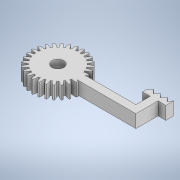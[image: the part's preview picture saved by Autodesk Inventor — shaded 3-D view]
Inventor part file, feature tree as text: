
AUTODESK INVENTOR PART (.ipt)
format: ipt  version: 2022 (Build 260153000, 153)  size: 456,704 bytes
history: native  units: in
note: dims shown in document units (in); Inventor stores cm internally (conversion verified against a paired STEP export)
features: extrude x16, sketch x16, pattern_circular x1
ambient origin geometry x8: Origin, YZ Plane, XZ Plane, XY Plane, X Axis, Y Axis, Z Axis, Center Point
bodies: Solid1 (feature_tree)
feature tree (33):
  extrude  "Extrusion1"  Depth=0.1575in
  pattern_circular  "Circular Pattern1"  Count=28 Angle=360.0deg
  extrude  "Extrusion6"  Depth=0.1969in
  extrude  "Extrusion7"  Depth=1.1811in
  extrude  "Extrusion8"  Depth=0.748in
  extrude  "Extrusion9"  Depth=0.1969in
  extrude  "Extrusion10"  Depth=0.0591in
  extrude  "Extrusion11"  Depth=0.0591in
  extrude  "Extrusion12"  Depth=0.3543in
  extrude  "Extrusion13"  Depth=0.1969in
  extrude  "Extrusion14"  Depth=0.1969in
  extrude  "Extrusion15"  Depth=0.1969in
  extrude  "Extrusion16"  Depth=0.1969in
  extrude  "Extrusion17"  Depth=0.1969in TaperAngle=0.0deg
  extrude  "Extrusion18"  Depth=0.1969in
  extrude  "Extrusion19"  Depth=0.3543in
  extrude  "Extrusion20"  Depth=0.1181in
  sketch  "Sketch1"  dims[d0=0.6299in d1=0.1575in]
  sketch  "Sketch8"  dims[d2=0.0098in]
  sketch  "Sketch9"  dims[d3=0.0098in]
  sketch  "Sketch10"  dims[d4=0.0236in]
  sketch  "Sketch11"  dims[d7=0.0472in]
  sketch  "Sketch12"  dims[d8=0.1772in]
  sketch  "Sketch13"  dims[d10=0.0787in]
  sketch  "Sketch14"  dims[d11=0.1969in d12=0.0in d13=11.0236in d14=360.0deg]
  sketch  "Sketch15"  dims[d49=0.1969in d50=0.1575in]
  sketch  "Sketch16"  dims[d51=0.5438in d52=0.0in d53=1.1811in]
  sketch  "Sketch17"  dims[d54=0.7087in d55=0.748in]
  sketch  "Sketch18"  dims[d56=0.748in d57=0.1969in]
  sketch  "Sketch19"  dims[d58=0.9843in d59=0.0591in]
  sketch  "Sketch20"  dims[d60=0.0591in d61=0.0591in]
  sketch  "Sketch21"  dims[d62=0.3543in d63=0.0591in]
  sketch  "Sketch22"  dims[d64=0.1181in d65=0.1969in d66=0.0197in d67=0.0197in d68=0.0197in d69=0.1969in d70=0.0in d71=1.1811in d72=0.3543in d73=0.1181in d74=0.1181in d75=0.3543in d76=0.1181in d77=0.1969in d78=0.0197in d79=0.1969in d80=0.0197in d81=0.0197in d82=0.1969in d83=0.0in d84=0.1811in d85=0.1969in d86=0.0in d87=0.4813in d88=0.0in d89=0.1181in d90=0.3543in d91=0.9843in d92=1.2205in d93=0.1181in d94=0.1181in d95=0.0787in d96=0.1969in d97=0.0in d98=0.0787in d99=0.0394in d100=0.4188in d101=0.0in d102=0.0394in d103=0.0394in d104=0.3937in d105=0.0in d106=0.1181in d107=0.0591in d108=0.6063in d109=0.0in d110=0.1181in d111=0.2756in d112=0.9843in d113=1.2205in d114=0.0787in d115=0.0787in d116=0.0394in d117=0.1969in d118=0.0in d119=0.3031in d120=0.0in d121=0.4469in d122=0.0in d123=0.0394in d124=0.0in d125=1.1811in d126=0.3937in d127=0.1181in d128=0.1181in d129=0.1181in d130=0.1181in d131=0.1181in d132=0.1181in d133=0.1969in d134=0.0in d135=0.0787in d136=0.5531in d137=0.0in]
